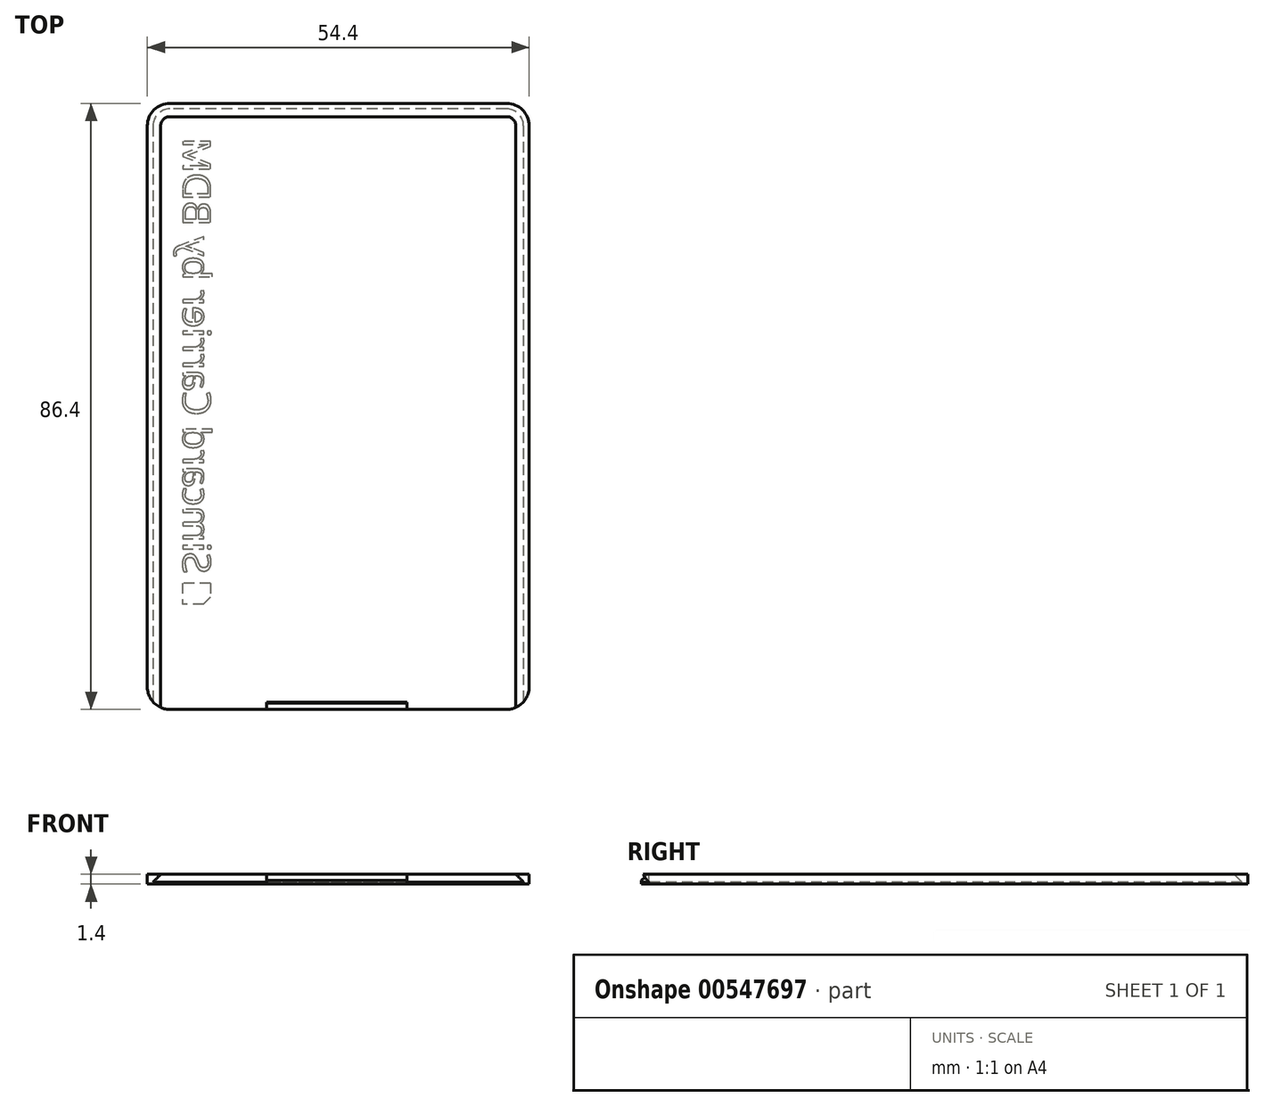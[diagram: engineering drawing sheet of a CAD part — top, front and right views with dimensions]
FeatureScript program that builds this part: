
annotation { "Feature Type Name" : "Feature", "Feature Type Description" : "" }
export const myFeature = defineFeature(function(context is Context, id is Id, definition is map)
    precondition{}
    {
        {
            var Q0;
            Q0=qCreatedBy(makeId("Front.planeOp"),FACE);
            var sketch = newSketch(context, id + "F0", { "sketchPlane" : qUnion([Q0])});
            skLineSegment(sketch, "E0", {"start": v(-3.2, 0) * mm, "end": v(0, 0) * mm});
            skLineSegment(sketch, "E1", {"start": v(0, 0) * mm, "end": v(0, 0.3) * mm});
            skLineSegment(sketch, "E2", {"start": v(0, 0.3) * mm, "end": v(-2.4, 0.3) * mm});
            skLineSegment(sketch, "E3", {"start": v(-2.4, 0.3) * mm, "end": v(-1.3, 1.4) * mm});
            skLineSegment(sketch, "E4", {"start": v(-1.3, 1.4) * mm, "end": v(-3.2, 1.4) * mm});
            skLineSegment(sketch, "E5", {"start": v(-3.2, 1.4) * mm, "end": v(-3.2, 0) * mm});
            skLineSegment(sketch, "E6", {"start": v(0, 0) * mm, "end": v(0, 1.12) * mm, "construction": true});
            skPoint(sketch, "E6.endSnap0", {"position": v(0, 0.15) * mm});
            skSolve(sketch);
        }
        {
            var Q0;
            Q0 = qSketchRegion(id + "F0", true);
            var Q1;
            Q1=sQuery(id+"F0.wireOp",EDGE,"E5");
            var Q2;
            Q2=sQuery(id+"F0.wireOp",EDGE,"E4");
            var Q3;
            Q3=sQuery(id+"F0.wireOp",EDGE,"E3");
            var Q4;
            Q4=sQuery(id+"F0.wireOp",EDGE,"E2");
            var Q5;
            Q5=sQuery(id+"F0.wireOp",EDGE,"E0");
            var Q6;
            Q6=sQuery(id+"F0.wireOp",EDGE,"E1");
            var Q7;
            Q7=sQuery(id+"F0.wireOp",EDGE,"E6");
            revolve(context, id + "F1", {"entities" : qUnion([Q0]), "surfaceEntities" : qUnion([Q1, Q2, Q3, Q4, Q5, Q6]), "axis" : qUnion([Q7]), "revolveType" : RevolveType.ONE_DIRECTION, "angle" : 90 * degree});
        }
        {
            var Q0;
            Q0=makeQuery(id+"F1.opRevolve","CAP_FACE",FACE,{"disambiguationData":[OSD([sQuery(id+"F0.wireOp",EDGE,"E0"),sQuery(id+"F0.wireOp",EDGE,"E1"),sQuery(id+"F0.wireOp",EDGE,"E2"),sQuery(id+"F0.wireOp",EDGE,"E3"),sQuery(id+"F0.wireOp",EDGE,"E4"),sQuery(id+"F0.wireOp",EDGE,"E5")])],"isStart":false});
            var sketch = newSketch(context, id + "F2", { "sketchPlane" : qUnion([Q0])});
            skLineSegment(sketch, "E7.0.0", {"start": v(-1.3, 1.4) * mm, "end": v(-3.2, 1.4) * mm});
            skLineSegment(sketch, "E7.0.1", {"start": v(-3.2, 1.4) * mm, "end": v(-3.2, 0) * mm});
            skLineSegment(sketch, "E7.0.2", {"start": v(-3.2, 0) * mm, "end": v(0, 0) * mm});
            skLineSegment(sketch, "E7.0.3", {"start": v(0, 0) * mm, "end": v(0, 0.3) * mm});
            skLineSegment(sketch, "E7.0.4", {"start": v(0, 0.3) * mm, "end": v(-2.4, 0.3) * mm});
            skLineSegment(sketch, "E7.0.5", {"start": v(-2.4, 0.3) * mm, "end": v(-1.3, 1.4) * mm});
            skSolve(sketch);
        }
        {
            var Q0;
            Q0 = qSketchRegion(id + "F2", true);
            extrude(context, id + "F3", {"entities" : qUnion([Q0]), "operationType" : NewBodyOperationType.ADD, "depth" : 24 * mm, "offsetDistance" : 25 * mm});
        }
        {
            var Q0;
            Q0=makeQuery(id+"F3.boolean.opBoolean","MERGE",FACE,{"derivedFrom":[makeQuery(id+"F1.opRevolve","CAP_FACE",FACE,{"disambiguationData":[OSD([sQuery(id+"F0.wireOp",EDGE,"E0"),sQuery(id+"F0.wireOp",EDGE,"E1"),sQuery(id+"F0.wireOp",EDGE,"E2"),sQuery(id+"F0.wireOp",EDGE,"E3"),sQuery(id+"F0.wireOp",EDGE,"E4"),sQuery(id+"F0.wireOp",EDGE,"E5")])],"isStart":true}),makeQuery(id+"F3.opExtrude","SWEPT_FACE",FACE,{"disambiguationData":[OSD([sQuery(id+"F2.wireOp",EDGE,"E7.0.3")])]})]});
            var sketch = newSketch(context, id + "F4", { "sketchPlane" : qUnion([Q0])});
            skLineSegment(sketch, "E8.0.0", {"start": v(3.2, 1.4) * mm, "end": v(1.3, 1.4) * mm});
            skLineSegment(sketch, "E8.0.1", {"start": v(1.3, 1.4) * mm, "end": v(2.4, 0.3) * mm});
            skLineSegment(sketch, "E8.0.2", {"start": v(2.4, 0.3) * mm, "end": v(-24, 0.3) * mm});
            skLineSegment(sketch, "E8.0.3", {"start": v(-24, 0.3) * mm, "end": v(-24, 0) * mm});
            skLineSegment(sketch, "E8.0.4", {"start": v(-24, 0) * mm, "end": v(3.2, 0) * mm});
            skLineSegment(sketch, "E8.0.5", {"start": v(3.2, 0) * mm, "end": v(3.2, 1.4) * mm});
            skSolve(sketch);
        }
        {
            var Q0;
            Q0 = qSketchRegion(id + "F4", true);
            extrude(context, id + "F5", {"entities" : qUnion([Q0]), "operationType" : NewBodyOperationType.ADD, "depth" : 40 * mm, "offsetDistance" : 25 * mm});
        }
        {
            var Q0;
            Q0=makeQuery(id+"F1.opRevolve","SWEPT_BODY",BODY,{"disambiguationData":[OSD([sQuery(id+"F0.wireOp",EDGE,"E0"),sQuery(id+"F0.wireOp",EDGE,"E1"),sQuery(id+"F0.wireOp",EDGE,"E2"),sQuery(id+"F0.wireOp",EDGE,"E3"),sQuery(id+"F0.wireOp",EDGE,"E4"),sQuery(id+"F0.wireOp",EDGE,"E5")])]});
            var Q1;
            Q1=makeQuery(id+"F5.boolean.opBoolean","MERGE",FACE,{"derivedFrom":[makeQuery(id+"F3.opExtrude","CAP_FACE",FACE,{"disambiguationData":[OSD([sQuery(id+"F2.wireOp",EDGE,"E7.0.0"),sQuery(id+"F2.wireOp",EDGE,"E7.0.1"),sQuery(id+"F2.wireOp",EDGE,"E7.0.2"),sQuery(id+"F2.wireOp",EDGE,"E7.0.3"),sQuery(id+"F2.wireOp",EDGE,"E7.0.4"),sQuery(id+"F2.wireOp",EDGE,"E7.0.5")])],"isStart":false}),makeQuery(id+"F5.opExtrude","SWEPT_FACE",FACE,{"disambiguationData":[OSD([sQuery(id+"F4.wireOp",EDGE,"E8.0.3")])]})]});
            mirror(context, id + "F6", {"operationType" : NewBodyOperationType.ADD, "entities" : qUnion([Q0]), "mirrorPlane" : qUnion([Q1])});
        }
        {
            var Q0;
            Q0=makeQuery(id+"F1.opRevolve","SWEPT_BODY",BODY,{"disambiguationData":[OSD([sQuery(id+"F0.wireOp",EDGE,"E0"),sQuery(id+"F0.wireOp",EDGE,"E1"),sQuery(id+"F0.wireOp",EDGE,"E2"),sQuery(id+"F0.wireOp",EDGE,"E3"),sQuery(id+"F0.wireOp",EDGE,"E4"),sQuery(id+"F0.wireOp",EDGE,"E5")])]});
            var Q1;
            {var subQ0=makeQuery(id+"F5.opExtrude","CAP_FACE",FACE,{"disambiguationData":[OSD([sQuery(id+"F4.wireOp",EDGE,"E8.0.0"),sQuery(id+"F4.wireOp",EDGE,"E8.0.1"),sQuery(id+"F4.wireOp",EDGE,"E8.0.2"),sQuery(id+"F4.wireOp",EDGE,"E8.0.3"),sQuery(id+"F4.wireOp",EDGE,"E8.0.4"),sQuery(id+"F4.wireOp",EDGE,"E8.0.5")])],"isStart":false});Q1=makeQuery(id+"F6.boolean.opBoolean","MERGE",FACE,{"derivedFrom":[subQ0,makeQuery(id+"F6.opPattern","COPY",FACE,{"derivedFrom":subQ0,"instanceName":"1"})]});}
            mirror(context, id + "F7", {"operationType" : NewBodyOperationType.ADD, "entities" : qUnion([Q0]), "mirrorPlane" : qUnion([Q1])});
        }
        {
            var Q0;
            {var subQ0=makeQuery(id+"F3.opExtrude","SWEPT_FACE",FACE,{"disambiguationData":[OSD([sQuery(id+"F2.wireOp",EDGE,"E7.0.1")])]});Q0=makeQuery(id+"F6.boolean.opBoolean","MERGE",FACE,{"derivedFrom":[subQ0,makeQuery(id+"F6.opPattern","COPY",FACE,{"derivedFrom":subQ0,"instanceName":"1"})]});}
            var sketch = newSketch(context, id + "F8", { "sketchPlane" : qUnion([Q0])});
            skLineSegment(sketch, "E9", {"start": v(24, 0) * mm, "end": v(24, 2.5) * mm, "construction": true});
            skPoint(sketch, "E9.endSnap0", {"position": v(24, 1.4) * mm});
            skLineSegment(sketch, "E10", {"start": v(24, 0.3) * mm, "end": v(-2.4, 0.3) * mm});
            skLineSegment(sketch, "E11", {"start": v(-2.4, 0.3) * mm, "end": v(-1.3, 1.4) * mm});
            skLineSegment(sketch, "E12", {"start": v(-1.3, 1.4) * mm, "end": v(24, 1.4) * mm});
            skLineSegment(sketch, "E13.MirrorCS", {"start": v(49.3, 1.4) * mm, "end": v(24, 1.4) * mm});
            skLineSegment(sketch, "E14.MirrorCS", {"start": v(24, 0.3) * mm, "end": v(50.4, 0.3) * mm});
            skLineSegment(sketch, "E15.MirrorCS", {"start": v(50.4, 0.3) * mm, "end": v(49.3, 1.4) * mm});
            skSolve(sketch);
        }
        {
            var Q0;
            Q0 = qSketchRegion(id + "F8", true);
            extrude(context, id + "F9", {"entities" : qUnion([Q0]), "operationType" : NewBodyOperationType.REMOVE, "oppositeDirection" : true, "depth" : 25 * mm, "offsetDistance" : 25 * mm});
        }
        {
            var Q0;
            {var subQ0=makeQuery(id+"F5.boolean.opBoolean","MERGE",FACE,{"derivedFrom":[makeQuery(id+"F3.boolean.opBoolean","MERGE",FACE,{"derivedFrom":[makeQuery(id+"F1.opRevolve","SWEPT_FACE",FACE,{"disambiguationData":[OSD([sQuery(id+"F0.wireOp",EDGE,"E2")])]}),makeQuery(id+"F3.opExtrude","SWEPT_FACE",FACE,{"disambiguationData":[OSD([sQuery(id+"F2.wireOp",EDGE,"E7.0.4")])]})]}),makeQuery(id+"F5.opExtrude","SWEPT_FACE",FACE,{"disambiguationData":[OSD([sQuery(id+"F4.wireOp",EDGE,"E8.0.2")])]})]});var subQ1=makeQuery(id+"F6.boolean.opBoolean","MERGE",FACE,{"derivedFrom":[subQ0,makeQuery(id+"F6.opPattern","COPY",FACE,{"derivedFrom":subQ0,"instanceName":"1"})]});Q0=makeQuery(id+"F9.boolean.opBoolean","MERGE",FACE,{"derivedFrom":[makeQuery(id+"F7.boolean.opBoolean","MERGE",FACE,{"derivedFrom":[subQ1,makeQuery(id+"F7.opPattern","COPY",FACE,{"derivedFrom":subQ1,"instanceName":"1"})]}),makeQuery(id+"F9.opExtrude","SWEPT_FACE",FACE,{"disambiguationData":[OSD([sQuery(id+"F8.wireOp",EDGE,"E10"),sQuery(id+"F8.wireOp",EDGE,"E14.MirrorCS")])]})]});}
            var sketch = newSketch(context, id + "F10", { "sketchPlane" : qUnion([Q0])});
            skLineSegment(sketch, "E16.bottom", {"start": v(13.8, -3.2) * mm, "end": v(33.8, -3.2) * mm});
            skLineSegment(sketch, "E16.top", {"start": v(13.8, -2.2) * mm, "end": v(33.8, -2.2) * mm});
            skLineSegment(sketch, "E16.left", {"start": v(13.8, -3.2) * mm, "end": v(13.8, -2.2) * mm});
            skLineSegment(sketch, "E16.right", {"start": v(33.8, -3.2) * mm, "end": v(33.8, -2.2) * mm});
            skSolve(sketch);
        }
        {
            var Q0;
            Q0=makeQuery(id+"F10.imprint","IMPRINT",FACE,{"disambiguationData":[TD([[makeQuery(id+"F10.imprint","IMPRINT",EDGE,{"derivedFrom":sQuery(id+"F10.wireOp",EDGE,"E16.bottom")}),-1.0]])]});
            var Q1;
            {var subQ0=makeQuery(id+"F5.boolean.opBoolean","MERGE",FACE,{"derivedFrom":[makeQuery(id+"F3.boolean.opBoolean","MERGE",FACE,{"derivedFrom":[makeQuery(id+"F1.opRevolve","SWEPT_FACE",FACE,{"disambiguationData":[OSD([sQuery(id+"F0.wireOp",EDGE,"E4")])]}),makeQuery(id+"F3.opExtrude","SWEPT_FACE",FACE,{"disambiguationData":[OSD([sQuery(id+"F2.wireOp",EDGE,"E7.0.0")])]})]}),makeQuery(id+"F5.opExtrude","SWEPT_FACE",FACE,{"disambiguationData":[OSD([sQuery(id+"F4.wireOp",EDGE,"E8.0.0")])]})]});var subQ1=makeQuery(id+"F6.boolean.opBoolean","MERGE",FACE,{"derivedFrom":[subQ0,makeQuery(id+"F6.opPattern","COPY",FACE,{"derivedFrom":subQ0,"instanceName":"1"})]});Q1=makeQuery(id+"F7.boolean.opBoolean","MERGE",FACE,{"derivedFrom":[subQ1,makeQuery(id+"F7.opPattern","COPY",FACE,{"derivedFrom":subQ1,"instanceName":"1"})]});}
            extrude(context, id + "F11", {"entities" : qUnion([Q0]), "operationType" : NewBodyOperationType.ADD, "endBound" : BoundingType.UP_TO_SURFACE, "depth" : 0.85 * mm, "endBoundEntityFace" : qUnion([Q1]), "offsetDistance" : 25 * mm});
        }
        {
            var Q0;
            Q0=makeQuery(id+"F11.opExtrude","CAP_EDGE",EDGE,{"disambiguationData":[OSD([sQuery(id+"F10.wireOp",EDGE,"E16.bottom")])],"isStart":false});
            var Q1;
            {var subQ0=makeQuery(id+"F5.boolean.opBoolean","MERGE",FACE,{"derivedFrom":[makeQuery(id+"F3.boolean.opBoolean","MERGE",FACE,{"derivedFrom":[makeQuery(id+"F1.opRevolve","SWEPT_FACE",FACE,{"disambiguationData":[OSD([sQuery(id+"F0.wireOp",EDGE,"E4")])]}),makeQuery(id+"F3.opExtrude","SWEPT_FACE",FACE,{"disambiguationData":[OSD([sQuery(id+"F2.wireOp",EDGE,"E7.0.0")])]})]}),makeQuery(id+"F5.opExtrude","SWEPT_FACE",FACE,{"disambiguationData":[OSD([sQuery(id+"F4.wireOp",EDGE,"E8.0.0")])]})]});var subQ1=makeQuery(id+"F6.boolean.opBoolean","MERGE",FACE,{"derivedFrom":[subQ0,makeQuery(id+"F6.opPattern","COPY",FACE,{"derivedFrom":subQ0,"instanceName":"1"})]});Q1=makeQuery(id+"F11.opExtrude","TWEAK_EDGE",EDGE,{"derivedFrom":[makeQuery(id+"F7.boolean.opBoolean","MERGE",FACE,{"derivedFrom":[subQ1,makeQuery(id+"F7.opPattern","COPY",FACE,{"derivedFrom":subQ1,"instanceName":"1"})]}),makeQuery(id+"F10.imprint","IMPRINT",EDGE,{"derivedFrom":sQuery(id+"F10.wireOp",EDGE,"E16.bottom")})]});}
            chamfer(context, id + "F12", {"entities" : qUnion([Q0, Q1]), "width" : 0.9 * mm, "tangentPropagation" : true});
        }
        {
            var Q0;
            {var subQ0=makeQuery(id+"F5.boolean.opBoolean","MERGE",FACE,{"derivedFrom":[makeQuery(id+"F3.boolean.opBoolean","MERGE",FACE,{"derivedFrom":[makeQuery(id+"F1.opRevolve","SWEPT_FACE",FACE,{"disambiguationData":[OSD([sQuery(id+"F0.wireOp",EDGE,"E0")])]}),makeQuery(id+"F3.opExtrude","SWEPT_FACE",FACE,{"disambiguationData":[OSD([sQuery(id+"F2.wireOp",EDGE,"E7.0.2")])]})]}),makeQuery(id+"F5.opExtrude","SWEPT_FACE",FACE,{"disambiguationData":[OSD([sQuery(id+"F4.wireOp",EDGE,"E8.0.4")])]})]});var subQ1=makeQuery(id+"F6.boolean.opBoolean","MERGE",FACE,{"derivedFrom":[subQ0,makeQuery(id+"F6.opPattern","COPY",FACE,{"derivedFrom":subQ0,"instanceName":"1"})]});Q0=makeQuery(id+"F7.boolean.opBoolean","MERGE",FACE,{"derivedFrom":[subQ1,makeQuery(id+"F7.opPattern","COPY",FACE,{"derivedFrom":subQ1,"instanceName":"1"})]});}
            var sketch = newSketch(context, id + "F13", { "sketchPlane" : qUnion([Q0])});
            skText(sketch, "E17", { "text": "Simcard Carrier by BDM", "fontName": "OpenSans-Regular.ttf"});
            const initialGuessF13  = {"E17": [0.00185, -0.01618, 0, -1, 0.004]};
            skSetInitialGuess(sketch, initialGuessF13);
            skSolve(sketch);
        }
        {
            var Q0;
            Q0 = qSketchRegion(id + "F13", true);
            extrude(context, id + "F14", {"entities" : qUnion([Q0]), "operationType" : NewBodyOperationType.REMOVE, "oppositeDirection" : true, "depth" : 0.1 * mm, "offsetDistance" : 25 * mm});
        }
        {
            var Q0;
            {var subQ4=makeQuery(id+"F1.opRevolve","SWEPT_FACE",FACE,{"disambiguationData":[OSD([sQuery(id+"F0.wireOp",EDGE,"E5")])]});var subQ6=makeQuery(id+"F5.boolean.opBoolean","MERGE",FACE,{"derivedFrom":[makeQuery(id+"F3.boolean.opBoolean","MERGE",FACE,{"derivedFrom":[makeQuery(id+"F1.opRevolve","SWEPT_FACE",FACE,{"disambiguationData":[OSD([sQuery(id+"F0.wireOp",EDGE,"E0")])]}),makeQuery(id+"F3.opExtrude","SWEPT_FACE",FACE,{"disambiguationData":[OSD([sQuery(id+"F2.wireOp",EDGE,"E7.0.2")])]})]}),makeQuery(id+"F5.opExtrude","SWEPT_FACE",FACE,{"disambiguationData":[OSD([sQuery(id+"F4.wireOp",EDGE,"E8.0.4")])]})]});var subQ7=makeQuery(id+"F6.boolean.opBoolean","MERGE",FACE,{"derivedFrom":[subQ6,makeQuery(id+"F6.opPattern","COPY",FACE,{"derivedFrom":subQ6,"instanceName":"1"})]});Q0=makeQuery(id+"F14.boolean.opBoolean","SPLIT",FACE,{"disambiguationData":[TD([subQ4])],"derivedFrom":makeQuery(id+"F7.boolean.opBoolean","MERGE",FACE,{"derivedFrom":[subQ7,makeQuery(id+"F7.opPattern","COPY",FACE,{"derivedFrom":subQ7,"instanceName":"1"})]})});}
            var sketch = newSketch(context, id + "F15", { "sketchPlane" : qUnion([Q0])});
            skLineSegment(sketch, "E18.bottom", {"start": v(5.8, -14.8) * mm, "end": v(1.8, -14.8) * mm});
            skLineSegment(sketch, "E18.top", {"start": v(4.8, -11.8) * mm, "end": v(1.8, -11.8) * mm});
            skLineSegment(sketch, "E18.left", {"start": v(5.8, -14.8) * mm, "end": v(5.8, -12.8) * mm});
            skLineSegment(sketch, "E18.right", {"start": v(1.8, -14.8) * mm, "end": v(1.8, -11.8) * mm});
            skLineSegment(sketch, "E19", {"start": v(5.8, -12.8) * mm, "end": v(4.8, -11.8) * mm});
            skSolve(sketch);
        }
        {
            var Q0;
            Q0 = qSketchRegion(id + "F15", true);
            extrude(context, id + "F16", {"entities" : qUnion([Q0]), "operationType" : NewBodyOperationType.REMOVE, "oppositeDirection" : true, "depth" : 0.1 * mm, "offsetDistance" : 25 * mm});
        }
    });
